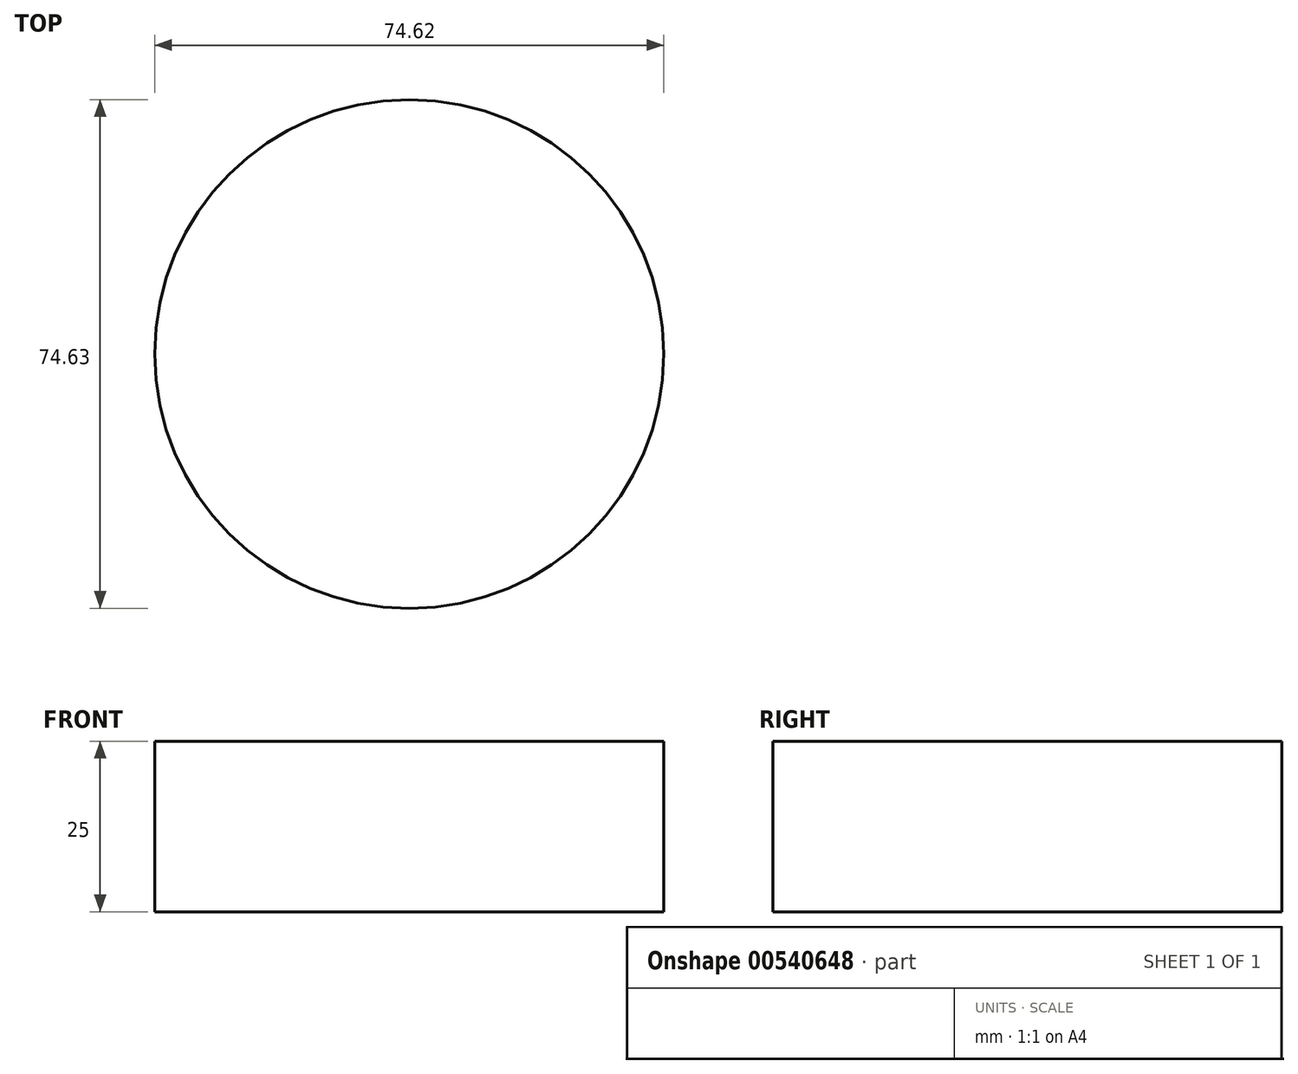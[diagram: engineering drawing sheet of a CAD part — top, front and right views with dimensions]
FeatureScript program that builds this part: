
annotation { "Feature Type Name" : "Feature", "Feature Type Description" : "" }
export const myFeature = defineFeature(function(context is Context, id is Id, definition is map)
    precondition{}
    {
        {
            var Q0;
            Q0=qCreatedBy(makeId("Top.planeOp"),FACE);
            var sketch = newSketch(context, id + "F0", { "sketchPlane" : qUnion([Q0])});
            skCircle(sketch, "E0", {"center": v(-42.7, -34.99) * mm, "radius": 37.31 * mm});
            skSolve(sketch);
        }
        {
            var Q0;
            Q0=makeQuery(id+"F0.imprint","IMPRINT",FACE,{"disambiguationData":[TD([[makeQuery(id+"F0.imprint","IMPRINT",EDGE,{"derivedFrom":sQuery(id+"F0.wireOp",EDGE,"E0")}),1.0]])]});
            extrude(context, id + "F1", {"entities" : qUnion([Q0]), "depth" : 25 * mm, "offsetDistance" : 25 * mm});
        }
    });
